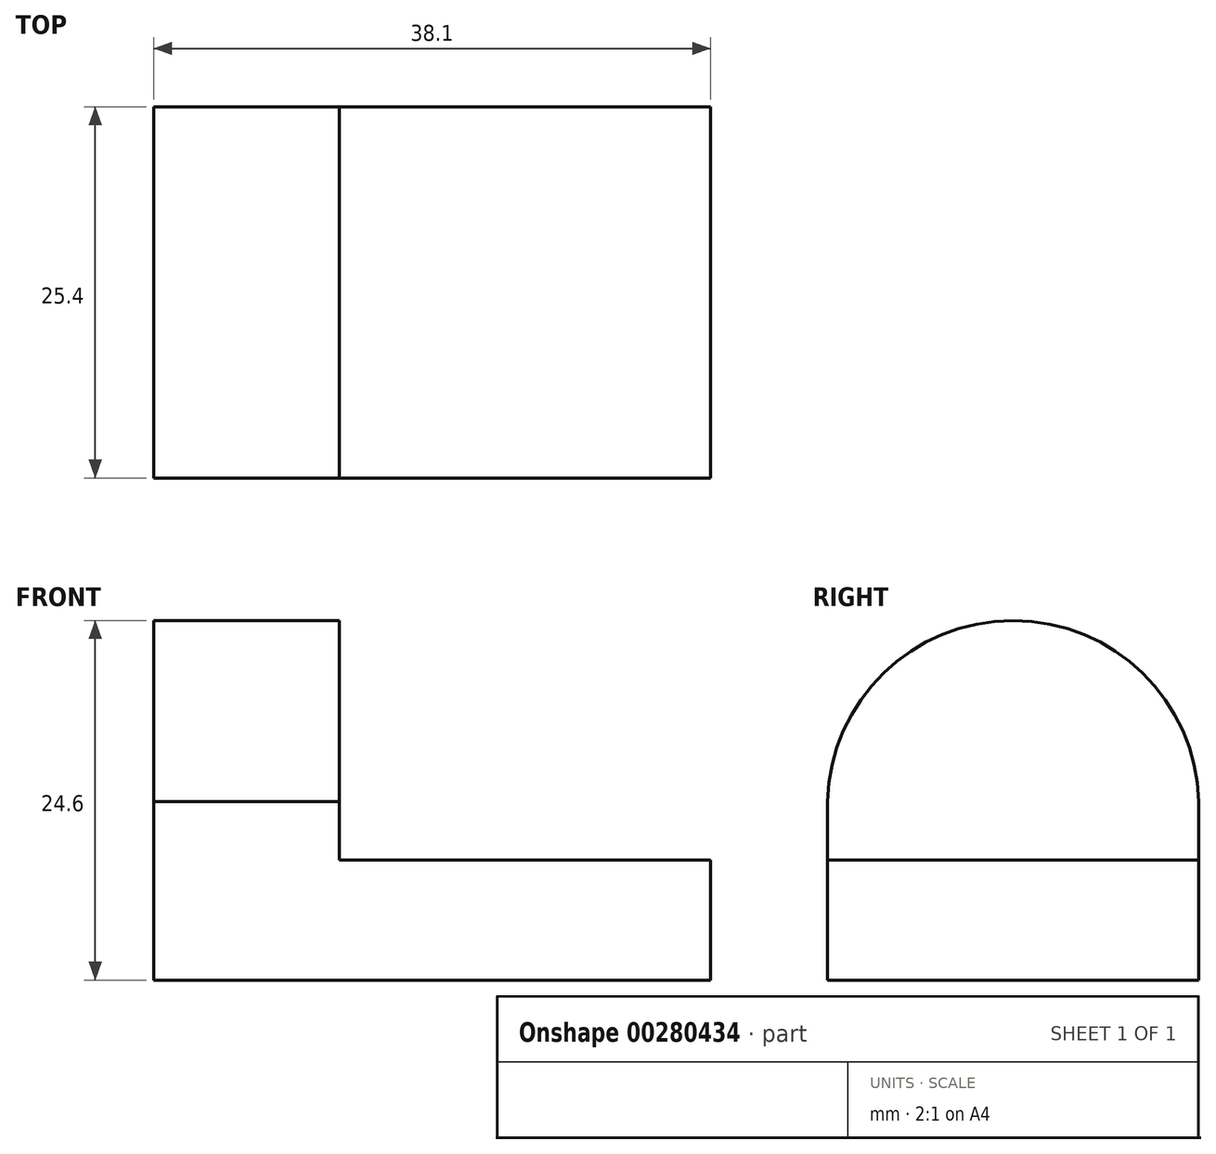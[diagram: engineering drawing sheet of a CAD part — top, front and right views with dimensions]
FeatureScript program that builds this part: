
annotation { "Feature Type Name" : "Feature", "Feature Type Description" : "" }
export const myFeature = defineFeature(function(context is Context, id is Id, definition is map)
    precondition{}
    {
        {
            var Q0;
            Q0=qCreatedBy(makeId("Front.planeOp"),FACE);
            var sketch = newSketch(context, id + "F0", { "sketchPlane" : qUnion([Q0])});
            skLineSegment(sketch, "E0", {"start": v(0, 0) * mm, "end": v(38.1, 0) * mm});
            skLineSegment(sketch, "E1", {"start": v(38.1, 0) * mm, "end": v(38.1, 25.4) * mm});
            skLineSegment(sketch, "E2", {"start": v(38.1, 25.4) * mm, "end": v(0, 25.4) * mm});
            skLineSegment(sketch, "E3", {"start": v(0, 25.4) * mm, "end": v(0, 0) * mm});
            skSolve(sketch);
        }
        {
            var Q0;
            Q0=qSketchRegion(id+"F0",true);
            extrude(context, id + "F1", {"entities" : qUnion([Q0]), "endBound" : BoundingType.SYMMETRIC, "depth" : 25.4 * mm});
        }
        {
            var Q0;
            Q0=makeQuery(id+"F1.opExtrude","CAP_FACE",FACE,{"disambiguationData":[OSD([sQuery(id+"F0.wireOp",EDGE,"E0"),sQuery(id+"F0.wireOp",EDGE,"E1"),sQuery(id+"F0.wireOp",EDGE,"E2"),sQuery(id+"F0.wireOp",EDGE,"E3")])],"isStart":false});
            var sketch = newSketch(context, id + "F2", { "sketchPlane" : qUnion([Q0])});
            skLineSegment(sketch, "E4", {"start": v(38.1, 8.22) * mm, "end": v(12.7, 8.22) * mm});
            skLineSegment(sketch, "E5", {"start": v(12.7, 8.22) * mm, "end": v(12.7, 25.4) * mm});
            skLineSegment(sketch, "E6", {"start": v(12.7, 25.4) * mm, "end": v(38.1, 25.4) * mm});
            skLineSegment(sketch, "E7", {"start": v(38.1, 25.4) * mm, "end": v(38.1, 8.22) * mm});
            skSolve(sketch);
        }
        {
            var Q0;
            Q0=makeQuery(id+"F2.imprint","IMPRINT",FACE,{"disambiguationData":[TD([[makeQuery(id+"F2.imprint","IMPRINT",EDGE,{"derivedFrom":sQuery(id+"F2.wireOp",EDGE,"E4")}),-1.0]])]});
            extrude(context, id + "F3", {"entities" : qUnion([Q0]), "operationType" : NewBodyOperationType.REMOVE, "endBound" : BoundingType.THROUGH_ALL, "oppositeDirection" : true, "depth" : 25.4 * mm});
        }
        {
            var Q0;
            Q0=makeQuery(id+"F1.opExtrude","SWEPT_FACE",FACE,{"disambiguationData":[OSD([sQuery(id+"F0.wireOp",EDGE,"E3")])]});
            var sketch = newSketch(context, id + "F4", { "sketchPlane" : qUnion([Q0])});
            skArc(sketch, "E8", {"start": v(12.7, 12.22) * mm, "mid": v(-0.33, 24.6) * mm, "end": v(-12.7, 11.57) * mm});
            skLineSegment(sketch, "E9", {"start": v(-12.7, 11.57) * mm, "end": v(-12.7, 25.4) * mm});
            skLineSegment(sketch, "E10", {"start": v(-12.7, 25.4) * mm, "end": v(12.7, 25.4) * mm});
            skLineSegment(sketch, "E11", {"start": v(12.7, 25.4) * mm, "end": v(12.7, 12.22) * mm});
            skSolve(sketch);
        }
        {
            var Q0;
            {var subQ4=sQuery(id+"F4.wireOp",EDGE,"E10");Q0=makeQuery(id+"F4.imprint","IMPRINT",FACE,{"disambiguationData":[TD([[makeQuery(id+"F4.imprint","IMPRINT",EDGE,{"derivedFrom":subQ4}),1.0]])]});}
            extrude(context, id + "F5", {"entities" : qUnion([Q0]), "operationType" : NewBodyOperationType.REMOVE, "endBound" : BoundingType.THROUGH_ALL, "oppositeDirection" : true, "depth" : 25.4 * mm});
        }
    });
